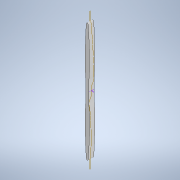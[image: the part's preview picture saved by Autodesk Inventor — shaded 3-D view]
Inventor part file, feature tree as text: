
AUTODESK INVENTOR PART (.ipt)
format: ipt  version: 2022 (Build 260153000, 153)  size: 1,655,808 bytes
history: native  units: mm
features: sketch x6, other x3, sweep x2, extrude x1, surface_op x1
ambient origin geometry x8: Origin, YZ Plane, XZ Plane, XY Plane, X Axis, Y Axis, Z Axis, Center Point
bodies: Solid1 (feature_tree)
feature tree (13):
  sketch  "Sketch1"  dims[d0=380.0mm d1=0.0mm d2=0.0mm]
  extrude  "Extrusion1"  TaperAngle=0.0deg  [1 undecoded]
  surface_op  "Stitch Surface1"
  sketch  "Sketch2"  dims[d3=380.0mm d4=90.0deg]
  sketch  "3D Sketch1"
  other  "Srf1"
  sketch  "Sketch3"  dims[d5=0.0mm d6=0.0mm d7=30.0mm d8=0.0mm]
  sketch  "3D Sketch2"
  other  "Srf2"
  sketch  "Sketch4"
  other  "Srf3"
  sweep  "SweepSrf1"
  sweep  "SweepSrf2"
note: 1 required parameter value undecoded (feature->parameter linkage not recoverable at this tier; creation-order binding heuristic only, values carry confidence <= 0.55)
